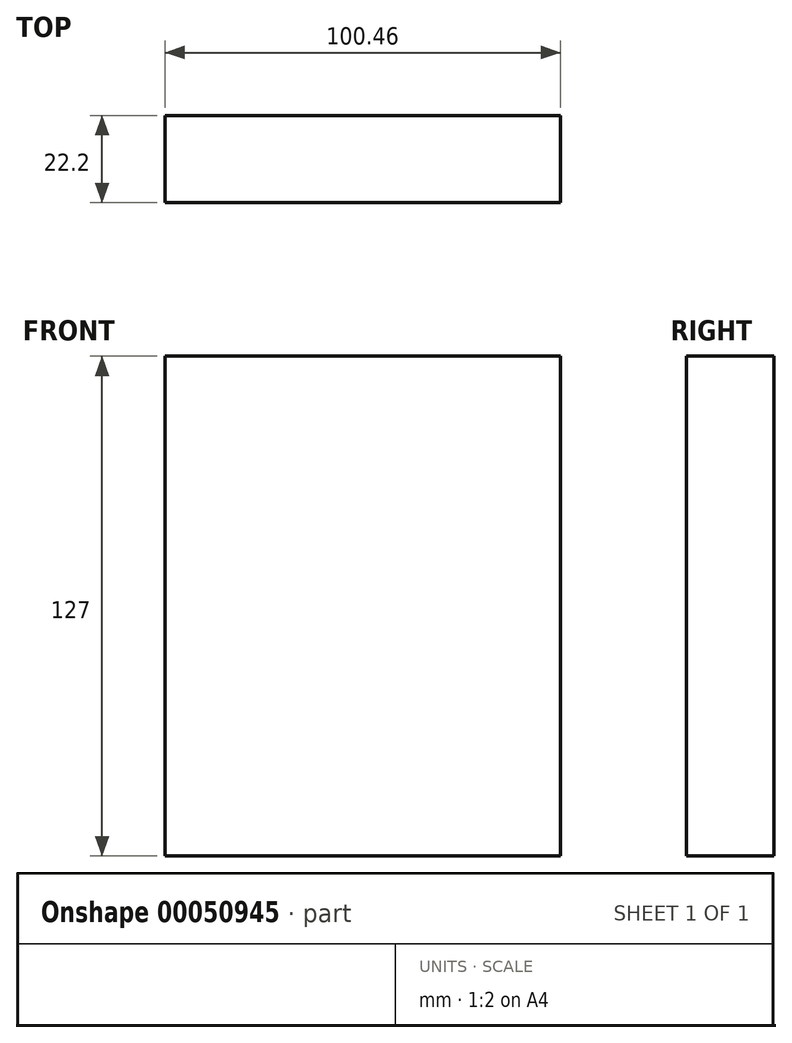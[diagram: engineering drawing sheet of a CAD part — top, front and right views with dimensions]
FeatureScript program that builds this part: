
annotation { "Feature Type Name" : "Feature", "Feature Type Description" : "" }
export const myFeature = defineFeature(function(context is Context, id is Id, definition is map)
    precondition{}
    {
        {
            var Q0;
            Q0=qCreatedBy(makeId("Top.planeOp"),FACE);
            var sketch = newSketch(context, id + "F0", { "sketchPlane" : qUnion([Q0])});
            skLineSegment(sketch, "E0.bottom", {"start": v(-50.23, -22.2) * mm, "end": v(0, -22.2) * mm});
            skLineSegment(sketch, "E0.top", {"start": v(-50.23, 0) * mm, "end": v(0, 0) * mm});
            skLineSegment(sketch, "E0.left", {"start": v(-50.23, -22.2) * mm, "end": v(-50.23, 0) * mm});
            skLineSegment(sketch, "E0.right", {"start": v(0, -22.2) * mm, "end": v(0, 0) * mm});
            skLineSegment(sketch, "E1.MirrorCS", {"start": v(50.23, 0) * mm, "end": v(0, 0) * mm});
            skLineSegment(sketch, "E2.MirrorCS", {"start": v(50.23, -22.2) * mm, "end": v(50.23, 0) * mm});
            skLineSegment(sketch, "E3.MirrorCS", {"start": v(50.23, -22.2) * mm, "end": v(0, -22.2) * mm});
            skSolve(sketch);
        }
        {
            var Q0;
            Q0 = qSketchRegion(id + "F0", true);
            extrude(context, id + "F1", {"entities" : qUnion([Q0]), "depth" : 127 * mm});
        }
    });
